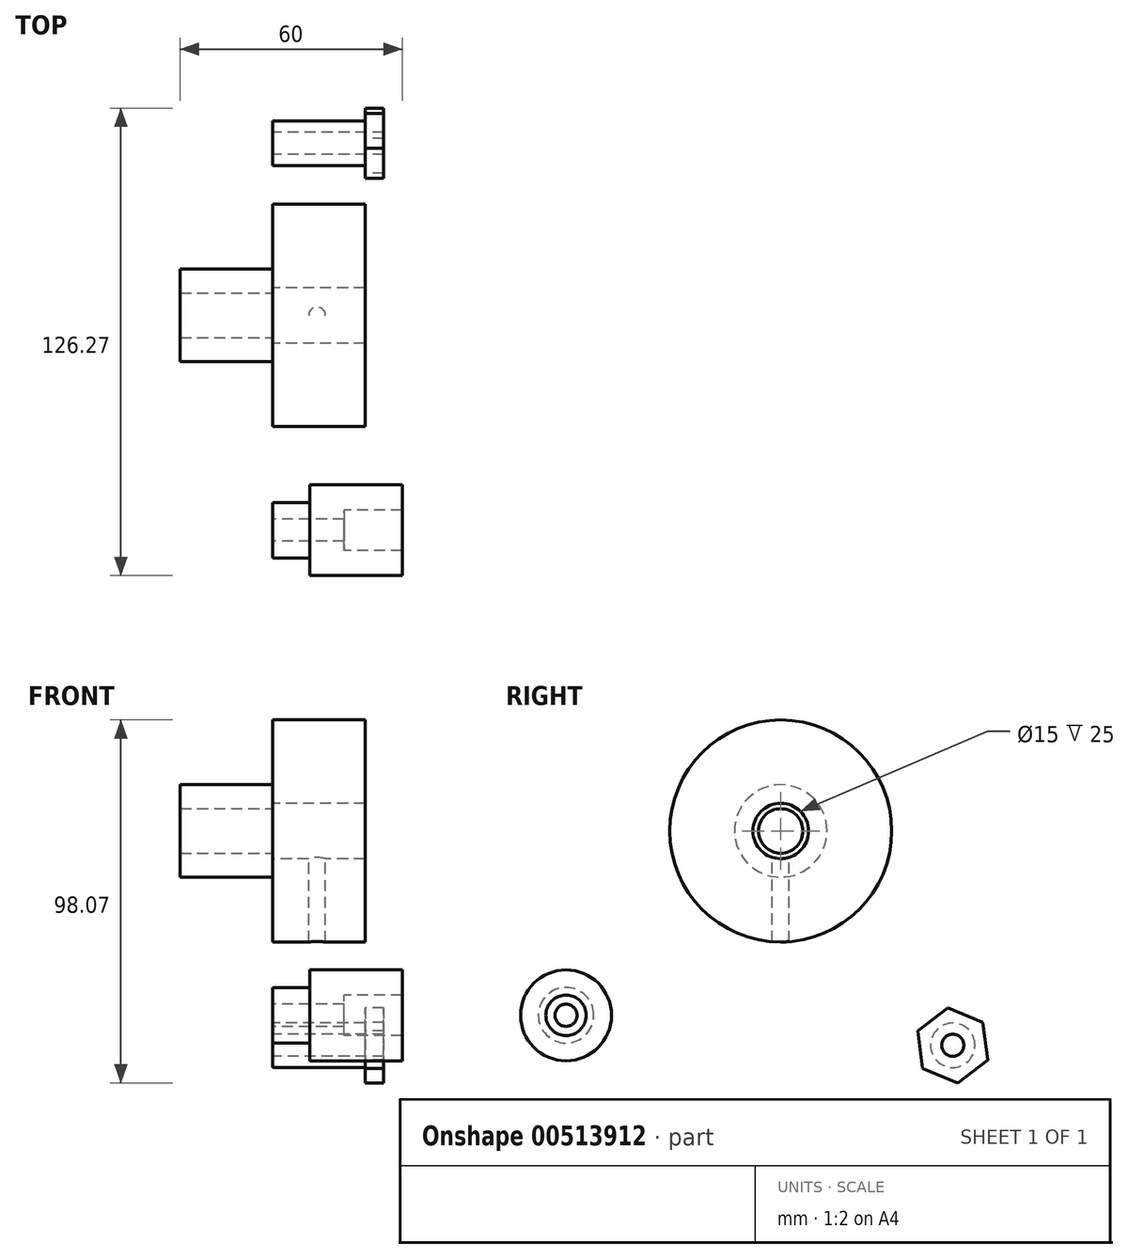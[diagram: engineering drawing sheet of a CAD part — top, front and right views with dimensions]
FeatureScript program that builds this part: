
annotation { "Feature Type Name" : "Feature", "Feature Type Description" : "" }
export const myFeature = defineFeature(function(context is Context, id is Id, definition is map)
    precondition{}
    {
        {
            var Q0;
            Q0=qCreatedBy(makeId("Right.planeOp"),FACE);
            var sketch = newSketch(context, id + "F0", { "sketchPlane" : qUnion([Q0])});
            skCircle(sketch, "E0", {"center": v(0, 0) * mm, "radius": 6 * mm});
            skCircle(sketch, "E1", {"center": v(0, 0) * mm, "radius": 30 * mm});
            skCircle(sketch, "E2", {"center": v(0, 0) * mm, "radius": 12.5 * mm});
            skSolve(sketch);
        }
        {
            var Q0;
            Q0=makeQuery(id+"F0.imprint","IMPRINT",FACE,{"disambiguationData":[TD([[makeQuery(id+"F0.imprint","IMPRINT",EDGE,{"derivedFrom":sQuery(id+"F0.wireOp",EDGE,"E0")}),-1.0]])]});
            extrude(context, id + "F1", {"entities" : qUnion([Q0]), "oppositeDirection" : true, "depth" : 25 * mm});
        }
        {
            var Q0;
            Q0=makeQuery(id+"F1.opExtrude","CAP_FACE",FACE,{"disambiguationData":[OSD([sQuery(id+"F0.wireOp",EDGE,"E0"),sQuery(id+"F0.wireOp",EDGE,"E2")])],"isStart":true});
            var sketch = newSketch(context, id + "F2", { "sketchPlane" : qUnion([Q0])});
            skCircle(sketch, "E3", {"center": v(0, 0) * mm, "radius": 7.5 * mm});
            skCircle(sketch, "E4", {"center": v(0, 0) * mm, "radius": 30 * mm});
            skSolve(sketch);
        }
        {
            var Q0;
            Q0 = qSketchRegion(id + "F2", true);
            extrude(context, id + "F3", {"entities" : qUnion([Q0]), "operationType" : NewBodyOperationType.ADD, "depth" : 25 * mm});
        }
        {
            var Q0;
            Q0=qCreatedBy(makeId("Top.planeOp"),FACE);
            var sketch = newSketch(context, id + "F4", { "sketchPlane" : qUnion([Q0])});
            skCircle(sketch, "E5", {"center": v(12, 0) * mm, "radius": 2.25 * mm});
            skSolve(sketch);
        }
        {
            var Q0;
            Q0 = qSketchRegion(id + "F4", true);
            extrude(context, id + "F5", {"entities" : qUnion([Q0]), "operationType" : NewBodyOperationType.REMOVE, "oppositeDirection" : true, "depth" : 36.7 * mm});
        }
        {
            var Q0;
            Q0=qCreatedBy(makeId("Right.planeOp"),FACE);
            var sketch = newSketch(context, id + "F6", { "sketchPlane" : qUnion([Q0])});
            skCircle(sketch, "E6", {"center": v(-58.03, -49.82) * mm, "radius": 7.5 * mm});
            skCircle(sketch, "E7", {"center": v(-58.03, -49.82) * mm, "radius": 3 * mm});
            skSolve(sketch);
        }
        {
            var Q0;
            Q0=makeQuery(id+"F6.imprint","IMPRINT",FACE,{"disambiguationData":[TD([[makeQuery(id+"F6.imprint","IMPRINT",EDGE,{"derivedFrom":sQuery(id+"F6.wireOp",EDGE,"E6")}),1.0]])]});
            extrude(context, id + "F7", {"entities" : qUnion([Q0]), "depth" : 10 * mm});
        }
        {
            var Q0;
            Q0=makeQuery(id+"F7.opExtrude","CAP_FACE",FACE,{"disambiguationData":[OSD([sQuery(id+"F6.wireOp",EDGE,"E6"),sQuery(id+"F6.wireOp",EDGE,"E7")])],"isStart":false});
            var sketch = newSketch(context, id + "F8", { "sketchPlane" : qUnion([Q0])});
            skCircle(sketch, "E8", {"center": v(-58.03, -49.82) * mm, "radius": 12.28 * mm});
            skCircle(sketch, "E9", {"center": v(-58.03, -49.82) * mm, "radius": 5.46 * mm});
            skSolve(sketch);
        }
        {
            var Q0;
            Q0 = qSketchRegion(id + "F8", true);
            extrude(context, id + "F9", {"entities" : qUnion([Q0]), "operationType" : NewBodyOperationType.ADD, "depth" : 25 * mm});
        }
        {
            var Q0;
            Q0=qCreatedBy(makeId("Right.planeOp"),FACE);
            var sketch = newSketch(context, id + "F10", { "sketchPlane" : qUnion([Q0])});
            skCircle(sketch, "E10", {"center": v(46.5, -57.92) * mm, "radius": 6 * mm});
            skCircle(sketch, "E11", {"center": v(46.5, -57.92) * mm, "radius": 3 * mm});
            skSolve(sketch);
        }
        {
            var Q0;
            Q0=makeQuery(id+"F10.imprint","IMPRINT",FACE,{"disambiguationData":[TD([[makeQuery(id+"F10.imprint","IMPRINT",EDGE,{"derivedFrom":sQuery(id+"F10.wireOp",EDGE,"E10")}),1.0]])]});
            extrude(context, id + "F11", {"entities" : qUnion([Q0]), "depth" : 25 * mm});
        }
        {
            var Q0;
            Q0=makeQuery(id+"F7.opExtrude","CAP_FACE",FACE,{"disambiguationData":[OSD([sQuery(id+"F6.wireOp",EDGE,"E6"),sQuery(id+"F6.wireOp",EDGE,"E7")])],"isStart":false});
            extrude(context, id + "F12", {"entities" : qUnion([Q0]), "operationType" : NewBodyOperationType.ADD, "depth" : 9.3 * mm});
        }
        {
            var Q0;
            Q0=makeQuery(id+"F11.opExtrude","CAP_FACE",FACE,{"disambiguationData":[OSD([sQuery(id+"F10.wireOp",EDGE,"E10"),sQuery(id+"F10.wireOp",EDGE,"E11")])],"isStart":false});
            var sketch = newSketch(context, id + "F13", { "sketchPlane" : qUnion([Q0])});
            skCircle(sketch, "E12.cCircle", {"center": v(46.5, -57.92) * mm, "radius": 12.72 * mm, "construction": true});
            skLineSegment(sketch, "E12.0", {"start": v(39.99, -71.08) * mm, "end": v(31.84, -58.86) * mm});
            skLineSegment(sketch, "E12.1", {"start": v(31.84, -58.86) * mm, "end": v(38.35, -45.7) * mm});
            skLineSegment(sketch, "E12.2", {"start": v(38.35, -45.7) * mm, "end": v(53, -44.76) * mm});
            skLineSegment(sketch, "E12.3", {"start": v(53, -44.76) * mm, "end": v(61.15, -56.98) * mm});
            skLineSegment(sketch, "E12.4", {"start": v(61.15, -56.98) * mm, "end": v(54.64, -70.14) * mm});
            skLineSegment(sketch, "E12.5", {"start": v(54.64, -70.14) * mm, "end": v(39.99, -71.08) * mm});
            skPoint(sketch, "E12.0.midPoint", {"position": v(35.92, -64.97) * mm});
            skSolve(sketch);
        }
        {
            var Q0;
            Q0=makeQuery(id+"F13.imprint","IMPRINT",FACE,{"disambiguationData":[TD([[makeQuery(id+"F13.imprint","IMPRINT",EDGE,{"derivedFrom":sQuery(id+"F13.wireOp",EDGE,"E12.0")}),-1.0]])]});
            extrude(context, id + "F14", {"entities" : qUnion([Q0]), "depth" : 9.4 * mm});
        }
        {
            var Q0;
            Q0=makeQuery(id+"F14.opExtrude","SWEPT_BODY",BODY,{"disambiguationData":[OSD([sQuery(id+"F10.wireOp",EDGE,"E10"),sQuery(id+"F13.wireOp",EDGE,"E12.0"),sQuery(id+"F13.wireOp",EDGE,"E12.1"),sQuery(id+"F13.wireOp",EDGE,"E12.2"),sQuery(id+"F13.wireOp",EDGE,"E12.3"),sQuery(id+"F13.wireOp",EDGE,"E12.4"),sQuery(id+"F13.wireOp",EDGE,"E12.5")])]});
            deleteBodies(context, id + "F15", {"entities" : qUnion([Q0])});
        }
        {
            var Q0;
            Q0=makeQuery(id+"F11.opExtrude","CAP_FACE",FACE,{"disambiguationData":[OSD([sQuery(id+"F10.wireOp",EDGE,"E10"),sQuery(id+"F10.wireOp",EDGE,"E11")])],"isStart":false});
            var sketch = newSketch(context, id + "F16", { "sketchPlane" : qUnion([Q0])});
            skCircle(sketch, "E13.cCircle", {"center": v(46.5, -57.92) * mm, "radius": 8.86 * mm, "construction": true});
            skLineSegment(sketch, "E13.0", {"start": v(55.96, -61.83) * mm, "end": v(47.84, -68.07) * mm});
            skLineSegment(sketch, "E13.1", {"start": v(47.84, -68.07) * mm, "end": v(38.38, -64.16) * mm});
            skLineSegment(sketch, "E13.2", {"start": v(38.38, -64.16) * mm, "end": v(37.04, -54) * mm});
            skLineSegment(sketch, "E13.3", {"start": v(37.04, -54) * mm, "end": v(45.16, -47.77) * mm});
            skLineSegment(sketch, "E13.4", {"start": v(45.16, -47.77) * mm, "end": v(54.61, -51.69) * mm});
            skLineSegment(sketch, "E13.5", {"start": v(54.61, -51.69) * mm, "end": v(55.96, -61.83) * mm});
            skPoint(sketch, "E13.0.midPoint", {"position": v(51.9, -64.95) * mm});
            skSolve(sketch);
        }
        {
            var Q0;
            Q0=makeQuery(id+"F16.imprint","IMPRINT",FACE,{"disambiguationData":[TD([[makeQuery(id+"F16.imprint","IMPRINT",EDGE,{"derivedFrom":sQuery(id+"F16.wireOp",EDGE,"E13.0")}),-1.0]])]});
            var Q1;
            Q1=makeQuery(id+"F16.imprint","IMPRINT",FACE,{"disambiguationData":[TD([[makeQuery(id+"F16.imprint","IMPRINT",EDGE,{"derivedFrom":makeQuery(id+"F11.opExtrude","CAP_EDGE",EDGE,{"disambiguationData":[OSD([sQuery(id+"F10.wireOp",EDGE,"E10")])],"isStart":false})}),1.0]])]});
            extrude(context, id + "F17", {"entities" : qUnion([Q0, Q1]), "operationType" : NewBodyOperationType.ADD, "depth" : 5 * mm});
        }
    });
